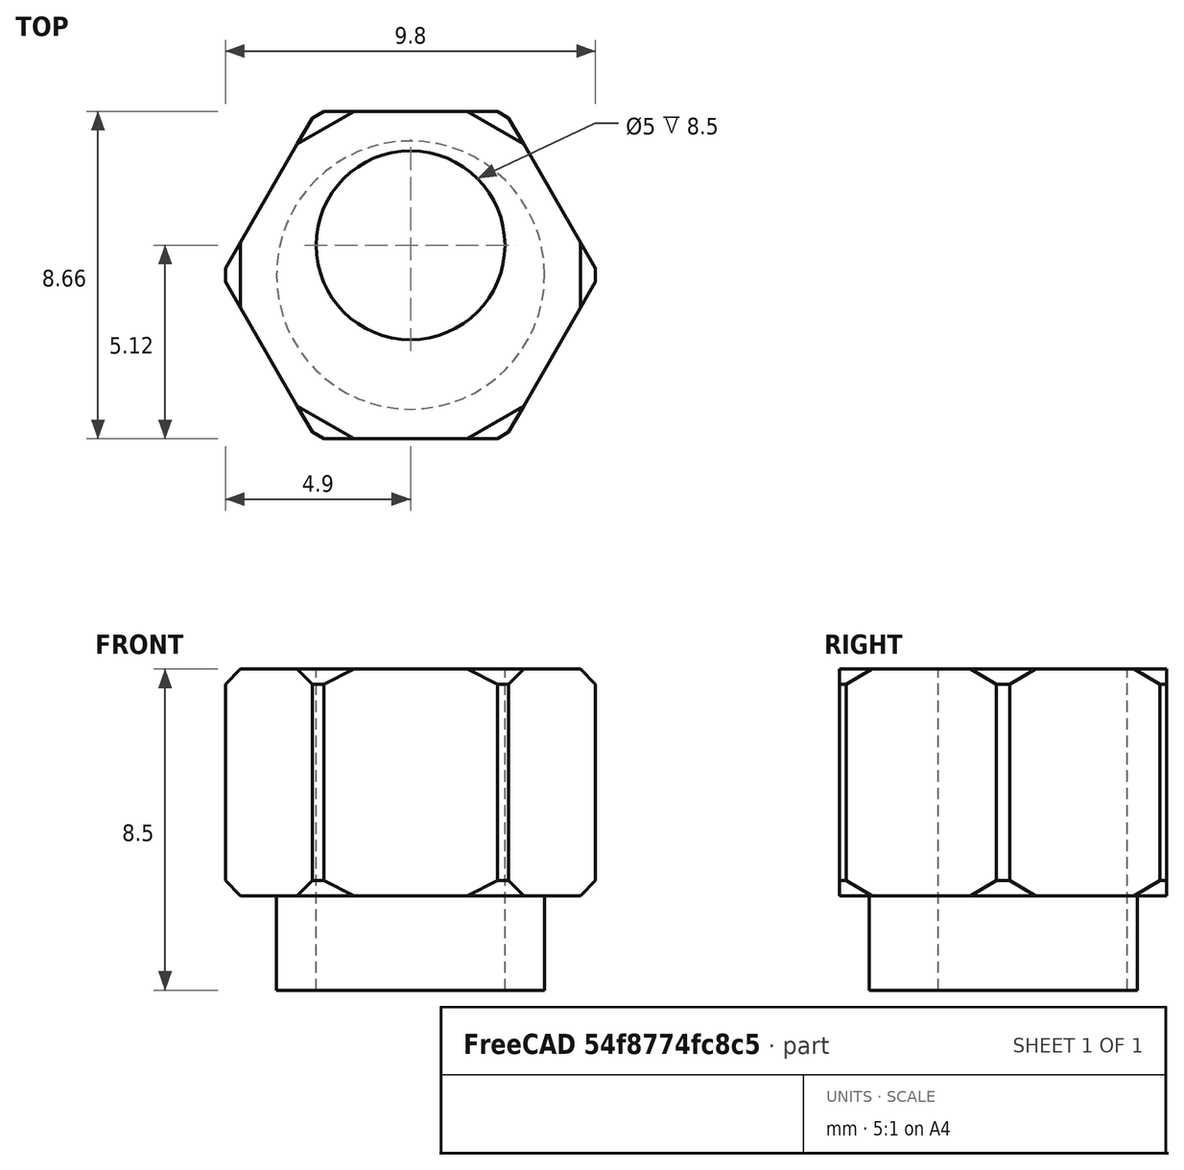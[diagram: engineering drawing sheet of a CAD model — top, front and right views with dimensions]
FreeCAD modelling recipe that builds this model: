
FCSTD DOCUMENT  (FreeCAD 0.19R23578 (Git))
Label: Sans nom1
License: All rights reserved
LicenseURL: http://en.wikipedia.org/wiki/All_rights_reserved
objects: Part::Cut×2, Part::Chamfer×2, Part::RegularPolygon×1, Part::FeaturePython×1, Part::Extrusion×1, Part::Cylinder×1
note: 8 computed .brp shape members not serialized (recipe doc carries the construction recipe); baked Part::Feature solids carry a one-line shape summary decoded from their .brp

FEATURE [Part::RegularPolygon] RegularPolygon  label="Polygone régulier"
  AttacherType = Attacher::AttachEngine3D
  Circumradius = 5
  Polygon = 6
FEATURE [Part::FeaturePython] Tube  # WARN: FeaturePython — macro-defined, semantics opaque (R4)
  AttacherType = Attacher::AttachEngine3D
  Height = 2.5
  InnerRadius = 3.55
  OuterRadius = 5
FEATURE [Part::Extrusion] Extrude
  Base = -> RegularPolygon
  Dir = (0,0,1)
  DirMode = 2
  FaceMakerClass = Part::FaceMakerBullseye
  LengthFwd = 8.5
  LengthRev = 0
  Solid = true
  Symmetric = false
FEATURE [Part::Cut] Cut
  Base = -> Extrude
  Tool = -> Tube
FEATURE [Part::Cylinder] Cylinder  label="Cylindre"
  Angle = 360
  AttacherType = Attacher::AttachEngine3D
  Height = 8.5
  Placement = pos=(0,0.79,0) rot=(0,0,1;0rad)
  Radius = 2.5
FEATURE [Part::Cut] Cut001
  Base = -> Cut
  Tool = -> Cylinder
FEATURE [Part::Chamfer] Chamfer
  Base = -> Cut001
  Edges = 6 edges r=0.2: [Edge2,Edge4,Edge11,Edge18,Edge19,Edge20]
FEATURE [Part::Chamfer] Chamfer001
  Base = -> Chamfer
  Edges = 12 edges r=0.4: [Edge6,Edge7,Edge9,Edge11,Edge13,Edge15,Edge17,Edge19,Edge22,Edge24,Edge26,Edge28]
